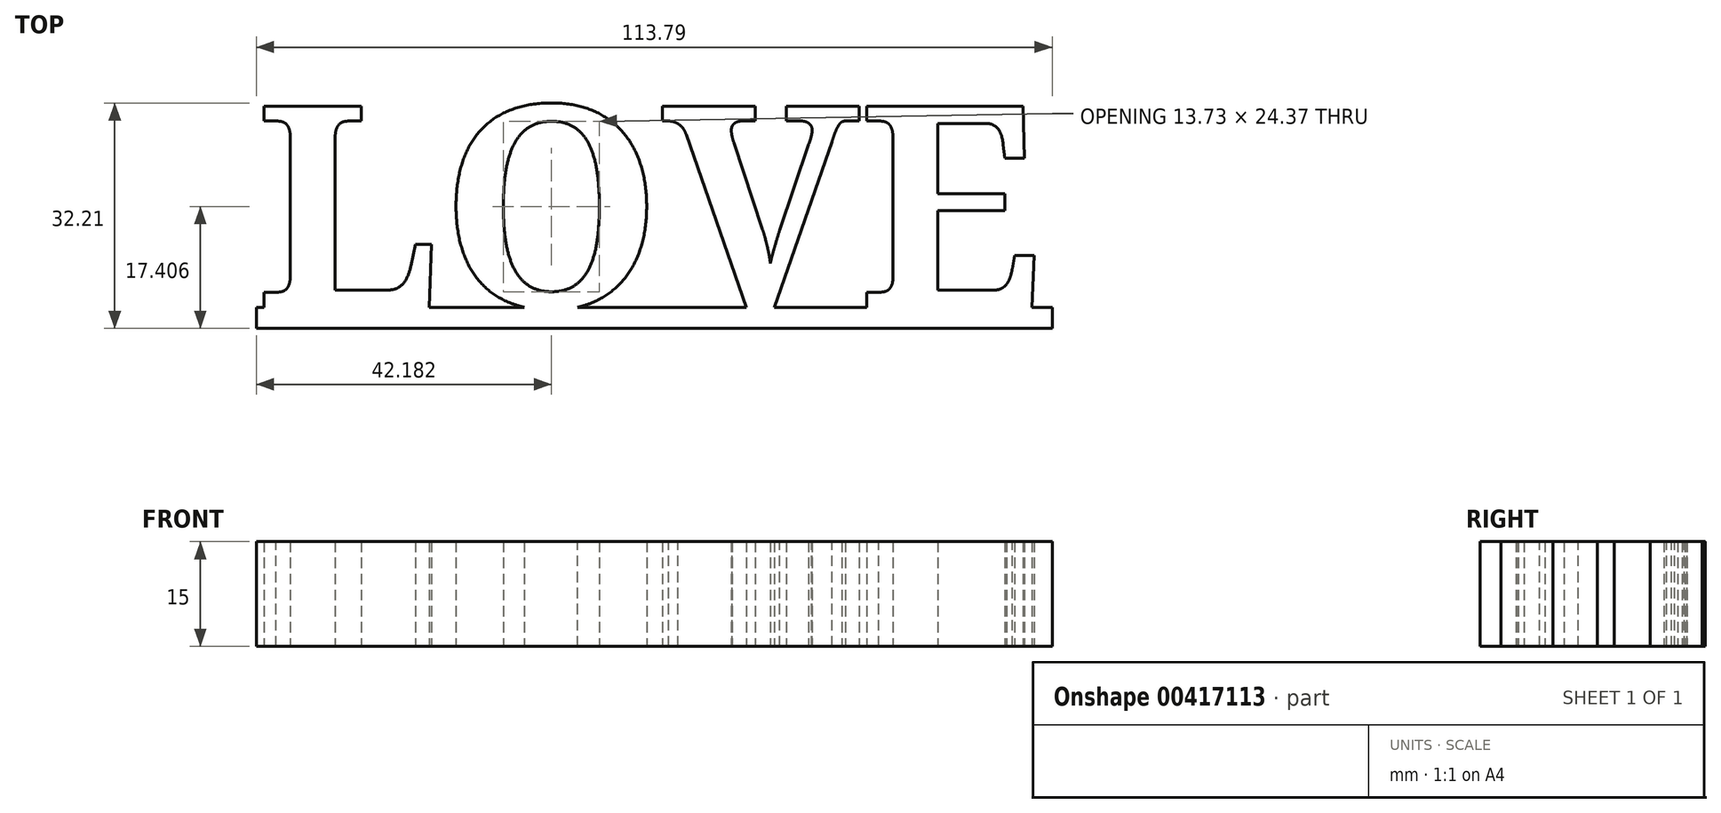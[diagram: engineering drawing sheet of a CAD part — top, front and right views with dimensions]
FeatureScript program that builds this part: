
annotation { "Feature Type Name" : "Feature", "Feature Type Description" : "" }
export const myFeature = defineFeature(function(context is Context, id is Id, definition is map)
    precondition{}
    {
        {
            var Q0;
            Q0=qCreatedBy(makeId("Top.planeOp"),FACE);
            var sketch = newSketch(context, id + "F0", { "sketchPlane" : qUnion([Q0])});
            skText(sketch, "E0", { "text": "LOVE", "fontName": "NotoSerif-Bold.ttf"});
            skLineSegment(sketch, "E1", {"start": v(0, 0) * mm, "end": v(113.8, 0) * mm});
            skLineSegment(sketch, "E2", {"start": v(113.8, 0) * mm, "end": v(113.8, -3) * mm});
            skLineSegment(sketch, "E3", {"start": v(113.8, -3) * mm, "end": v(0, -3) * mm});
            skLineSegment(sketch, "E4", {"start": v(0, -3) * mm, "end": v(0, 0) * mm});
            const initialGuessF0  = {"E0": [0, 0, 1, 0, 0.029]};
            skSetInitialGuess(sketch, initialGuessF0);
            skSolve(sketch);
        }
        {
            var Q0;
            Q0 = qSketchRegion(id + "F0", true);
            extrude(context, id + "F1", {"entities" : qUnion([Q0]), "depth" : 15 * mm});
        }
    });
